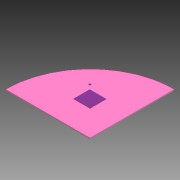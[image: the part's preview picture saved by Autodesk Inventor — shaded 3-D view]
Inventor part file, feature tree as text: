
AUTODESK INVENTOR PART (.ipt)
format: ipt  version: 2011 SP1 (Build 150282100, 282)  size: 125,440 bytes
history: native  units: mm
features: extrude x3, sketch x3, fillet x1, projected_geometry x1
ambient origin geometry x8: Origin, YZ Plane, XZ Plane, XY Plane, X Axis, Y Axis, Z Axis, Center Point
bodies: Solid1 (feature_tree)
feature tree (8):
  extrude  "Wafer"  Depth=0.525mm TaperAngle=0.0deg
  fillet  "OutsideEdge"  Radius=0.1mm
  extrude  "Wax"  Depth=20.0mm
  extrude  "Cutout"  Depth=9.0mm
  sketch  "Sketch1"  dims[d0=50.0mm d1=0.525mm d2=0.0mm d5=0.1mm]
  sketch  "Sketch3"  dims[d6=0.25mm d7=0.0mm d8=20.0mm]
  sketch  "Sketch4"  dims[d9=20.0mm d10=9.0mm d11=10.0mm d12=0.1mm d13=-10.053096mm d14=0.5mm d15=2.5mm d16=2.5mm]
  projected_geometry  "Projected Loop1"
